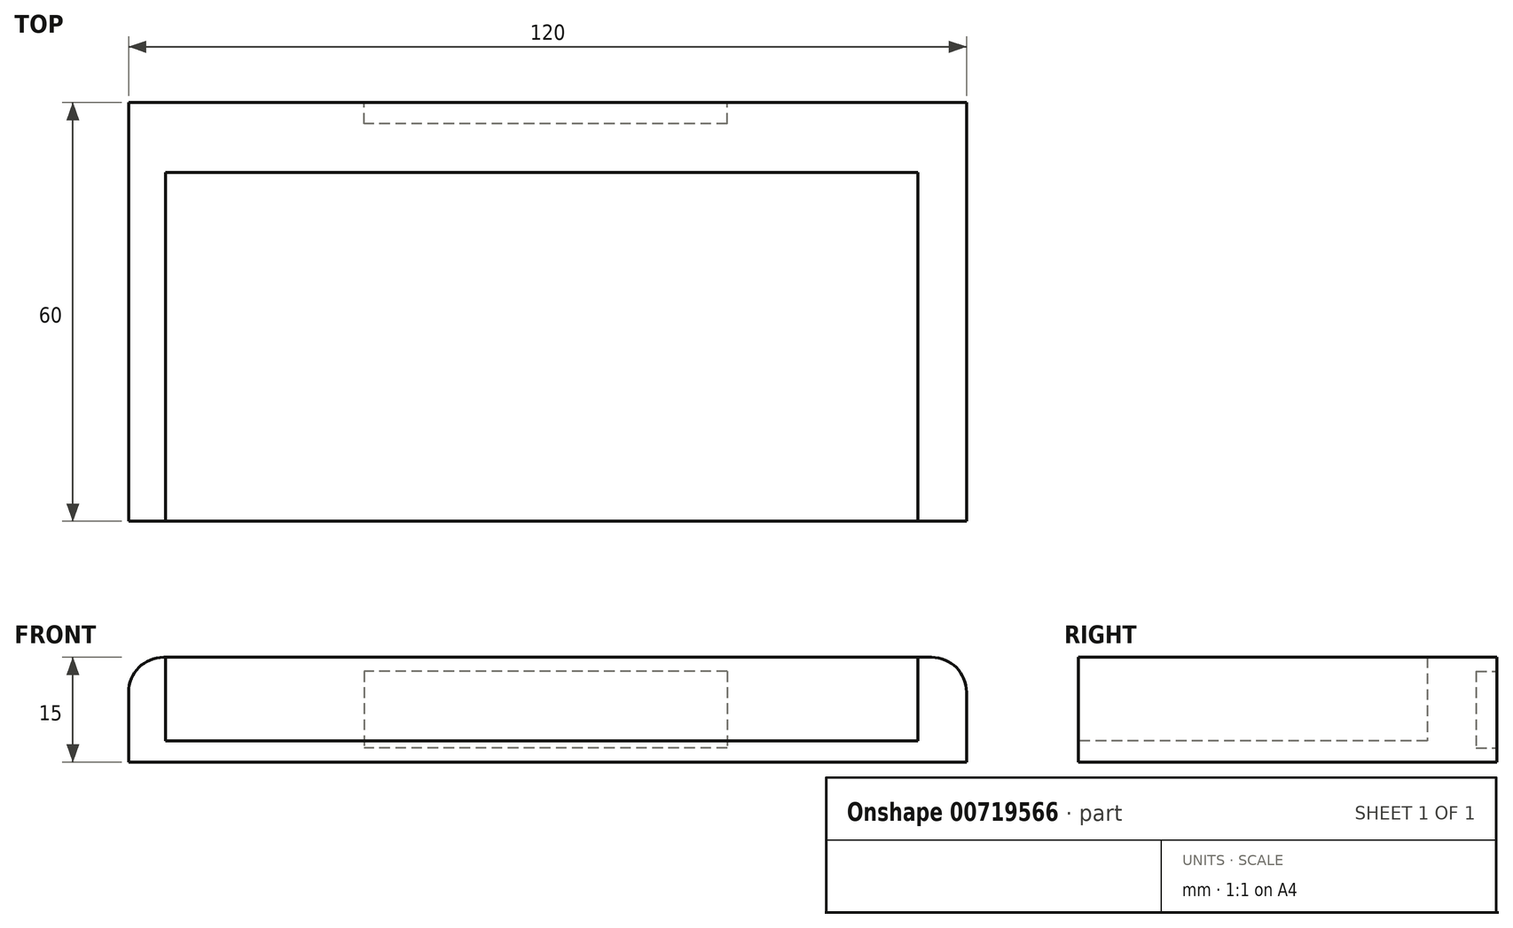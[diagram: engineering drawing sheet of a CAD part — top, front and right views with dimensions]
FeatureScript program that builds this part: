
annotation { "Feature Type Name" : "Feature", "Feature Type Description" : "" }
export const myFeature = defineFeature(function(context is Context, id is Id, definition is map)
    precondition{}
    {
        {
            var Q0;
            Q0=qCreatedBy(makeId("Top.planeOp"),FACE);
            var sketch = newSketch(context, id + "F0", { "sketchPlane" : qUnion([Q0])});
            skLineSegment(sketch, "E0.top", {"start": v(-57.71, -50) * mm, "end": v(62.29, -50) * mm});
            skLineSegment(sketch, "E0.left", {"start": v(-57.71, 0) * mm, "end": v(-57.71, -50) * mm});
            skLineSegment(sketch, "E0.right", {"start": v(62.29, 0) * mm, "end": v(62.29, -50) * mm});
            skLineSegment(sketch, "E1", {"start": v(55.35, -50) * mm, "end": v(55.35, 0) * mm});
            skLineSegment(sketch, "E2", {"start": v(-52.44, -50) * mm, "end": v(-52.44, -50) * mm});
            skLineSegment(sketch, "E3.bottom", {"start": v(-52.44, 0) * mm, "end": v(55.35, 0) * mm});
            skLineSegment(sketch, "E3.top", {"start": v(-57.71, 10) * mm, "end": v(62.29, 10) * mm});
            skLineSegment(sketch, "E3.left", {"start": v(-57.71, 0) * mm, "end": v(-57.71, 10) * mm});
            skLineSegment(sketch, "E3.right", {"start": v(62.29, 0) * mm, "end": v(62.29, 10) * mm});
            skLineSegment(sketch, "E4", {"start": v(-52.44, -50) * mm, "end": v(-52.44, 0) * mm});
            skSolve(sketch);
        }
        {
            var Q0;
            {var subQ0=sQuery(id+"F0.wireOp",EDGE,"E0.left");Q0=makeQuery(id+"F0.imprint","IMPRINT",FACE,{"disambiguationData":[TD([[makeQuery(id+"F0.imprint","IMPRINT",EDGE,{"derivedFrom":subQ0}),1.0]])]});}
            var Q1;
            {var subQ0=sQuery(id+"F0.wireOp",EDGE,"E0.right");Q1=makeQuery(id+"F0.imprint","IMPRINT",FACE,{"disambiguationData":[TD([[makeQuery(id+"F0.imprint","IMPRINT",EDGE,{"derivedFrom":subQ0}),-1.0]])]});}
            var Q2;
            Q2=makeQuery(id+"F0.imprint","IMPRINT",FACE,{"disambiguationData":[TD([[makeQuery(id+"F0.imprint","IMPRINT",EDGE,{"derivedFrom":sQuery(id+"F0.wireOp",EDGE,"E3.top")}),-1.0]])]});
            var Q3;
            {var subQ0=sQuery(id+"F0.wireOp",EDGE,"E1");Q3=makeQuery(id+"F0.imprint","IMPRINT",FACE,{"disambiguationData":[TD([[makeQuery(id+"F0.imprint","IMPRINT",EDGE,{"derivedFrom":subQ0}),1.0]])]});}
            extrude(context, id + "F1", {"entities" : qUnion([Q0, Q1, Q2, Q3]), "depth" : 3 * mm, "offsetDistance" : 25 * mm});
        }
        {
            var Q0;
            Q0=makeQuery(id+"F0.imprint","IMPRINT",FACE,{"disambiguationData":[TD([[makeQuery(id+"F0.imprint","IMPRINT",EDGE,{"derivedFrom":sQuery(id+"F0.wireOp",EDGE,"E3.top")}),-1.0]])]});
            extrude(context, id + "F2", {"entities" : qUnion([Q0]), "depth" : 15 * mm, "offsetDistance" : 25 * mm});
        }
        {
            var Q0;
            Q0=makeQuery(id+"F2.opExtrude","CAP_EDGE",EDGE,{"disambiguationData":[OSD([sQuery(id+"F0.wireOp",EDGE,"E3.left")])],"isStart":false});
            var Q1;
            Q1=makeQuery(id+"F2.opExtrude","CAP_EDGE",EDGE,{"disambiguationData":[OSD([sQuery(id+"F0.wireOp",EDGE,"E3.right")])],"isStart":false});
            var Q2;
            Q2=makeQuery(id+"F1.opExtrude","SWEPT_EDGE",EDGE,{"disambiguationData":[OSD([sQuery(id+"F0.wireOp",EDGE,"E0.top"),sQuery(id+"F0.wireOp",EDGE,"E0.left")])]});
            var Q3;
            Q3=makeQuery(id+"F1.opExtrude","SWEPT_EDGE",EDGE,{"disambiguationData":[OSD([sQuery(id+"F0.wireOp",EDGE,"E0.top"),sQuery(id+"F0.wireOp",EDGE,"E0.right")])]});
            fillet(context, id + "F3", {"entities" : qUnion([Q0, Q1, Q2, Q3]), "radius" : 5 * mm, "tangentPropagation" : true, "allowEdgeOverflow" : false});
        }
        {
            var Q0;
            Q0=makeQuery(id+"F1.opExtrude","SWEPT_BODY",BODY,{"disambiguationData":[OSD([sQuery(id+"F0.wireOp",EDGE,"E0.top"),sQuery(id+"F0.wireOp",EDGE,"E0.left"),sQuery(id+"F0.wireOp",EDGE,"E0.right"),sQuery(id+"F0.wireOp",EDGE,"E3.top"),sQuery(id+"F0.wireOp",EDGE,"E3.left"),sQuery(id+"F0.wireOp",EDGE,"E3.right")])]});
            var Q1;
            Q1=makeQuery(id+"F2.opExtrude","SWEPT_BODY",BODY,{"disambiguationData":[OSD([sQuery(id+"F0.wireOp",EDGE,"E0.top"),sQuery(id+"F0.wireOp",EDGE,"E0.left"),sQuery(id+"F0.wireOp",EDGE,"E0.right"),sQuery(id+"F0.wireOp",EDGE,"E1"),sQuery(id+"F0.wireOp",EDGE,"E3.top"),sQuery(id+"F0.wireOp",EDGE,"E3.left"),sQuery(id+"F0.wireOp",EDGE,"E3.right"),sQuery(id+"F0.wireOp",EDGE,"E3.bottom"),sQuery(id+"F0.wireOp",EDGE,"E4")])]});
            booleanBodies(context, id + "F4", {"operationType" : BooleanOperationType.UNION, "tools" : qUnion([Q0, Q1])});
        }
        {
            var Q0;
            {var subQ0=sQuery(id+"F0.wireOp",EDGE,"E3.top");Q0=makeQuery(id+"F4.opBoolean","MERGE",FACE,{"derivedFrom":[makeQuery(id+"F1.opExtrude","SWEPT_FACE",FACE,{"disambiguationData":[OSD([subQ0])]}),makeQuery(id+"F2.opExtrude","SWEPT_FACE",FACE,{"disambiguationData":[OSD([subQ0])]})]});}
            var sketch = newSketch(context, id + "F5", { "sketchPlane" : qUnion([Q0])});
            skLineSegment(sketch, "E5.bottom", {"start": v(-28, 13) * mm, "end": v(24, 13) * mm});
            skLineSegment(sketch, "E5.top", {"start": v(-28, 2) * mm, "end": v(24, 2) * mm});
            skLineSegment(sketch, "E5.left", {"start": v(-28, 13) * mm, "end": v(-28, 2) * mm});
            skLineSegment(sketch, "E5.right", {"start": v(24, 13) * mm, "end": v(24, 2) * mm});
            skSolve(sketch);
        }
        {
            var Q0;
            Q0=makeQuery(id+"F5.imprint","IMPRINT",FACE,{"disambiguationData":[TD([[makeQuery(id+"F5.imprint","IMPRINT",EDGE,{"derivedFrom":sQuery(id+"F5.wireOp",EDGE,"E5.bottom")}),-1.0]])]});
            extrude(context, id + "F6", {"entities" : qUnion([Q0]), "operationType" : NewBodyOperationType.REMOVE, "oppositeDirection" : true, "depth" : 3 * mm, "offsetDistance" : 25 * mm});
        }
    });
